# Revit family: Краны шаровые с ЭИМ DN25-50, PN16
name_source: partatom
category: Арматура трубопроводов
revit_build: Autodesk Revit 2015 (Build: 20140322_1515(x64)
units: mm (PartAtom-declared; Revit-internal decimal feet)

## types (4) — shared parameters
URL = http://vogez.by
Видимость клапана = Да
Высота болтов площадки = 6 мм
Высота штока_1 = 25 мм
Высота штока_2 = 70 мм
Диаметр направляющих = 10 мм
Диаметр отверстий = 65 мм
Диаметр патрубка_2 = 45 мм
Диаметр площадки привода_1 = 80 мм
Диаметр площадки привода_2 = 35 мм
Диаметр присоединения привода = 40 мм
Диаметр присоединения провода = 15 мм
Диаметр штока_1 = 30 мм
Диаметр штока_2 = 8 мм
Длина пластины = 112 мм
Изготовитель = ООО "ВОГЕЗЭНЕРГО"
Максимальная температура среды = 150 °C
Материал и цвет корпуса крана = Сталь, неокрашенная
Материал и цвет остальных элементов = Сталь, неокрашенная
Материал и цвет привода = Пластик, черный
Межосевое направляющих = 65 мм
Наименование = Кран шаровой запорно-регулирующий с ЭИМ
Напряжение питания = 220 В
Номинальное время полного хода ВЭП = 90 c
Номинальное давление PN = 1.6 МПа
Номинальное число оборотов = 0.25
Основание пластины = 20 мм
Потребляемая мощность = 15 Вт
Рабочая среда = вода
Расстояние до оси привода_1 = 42 мм
Расстояние до оси привода_2 = 133 мм
Режим работы = повторно-кратковременный, ПВ не более 25%
Сигнал управления = трёхпозиционный
Скругления привода = 25 мм
Степень защиты = IP54
Толщиина пластины = 5 мм
Частота сети = 50 Гц
Ширина пластины = 30 мм
Ширина площадки = 20 мм
Ширина привода = 112 мм

## per-type parameters (varying)
| type | DN | Высота клапана | Высота направляющих | Высота основания привода | Высота посадки привода | Высота с приводом | Диаметр зеркала | Диаметр патрубка_1 | Диаметр узла смешивания | Диаметр фланца | Длина площадки | Масса с приводом | Обозначение | Радиус зеркала | Радиус условный | Радиус фланца | Строительная длина | Тип, марка | Толщина зеркала | Толщина фланца |
| Кран шаровой ВКШР с ЭИМ DN25, PN16 | 25 мм | 30 мм | 75 мм | 85 мм | 35 мм | 155 мм | 71 мм | 50 мм | 68 мм | 120 мм | 58 мм | 7.00 kg | ВКШР DN25 | 36 мм | 13 мм | 60 мм | 160 мм | ВКШР DN25 | 2 мм | 16 мм |
| Кран шаровой ВКШР с ЭИМ DN32, PN16 | 32 мм | 34 мм | 79 мм | 89 мм | 39 мм | 159 мм | 82 мм | 57 мм | 75 мм | 135 мм | 65 мм | 8.00 kg | ВКШР DN32 | 41 мм | 16 мм | 68 мм | 180 мм | ВКШР DN32 | 2 мм | 16 мм |
| Кран шаровой ВКШР с ЭИМ DN40, PN16 | 40 мм | 38 мм | 83 мм | 93 мм | 43 мм | 163 мм | 92 мм | 65 мм | 83 мм | 145 мм | 73 мм | 9.50 kg | ВКШР DN40 | 46 мм | 20 мм | 73 мм | 200 мм | ВКШР DN40 | 3 мм | 17 мм |
| Кран шаровой ВКШР с ЭИМ DN50, PN16 | 50 мм | 43 мм | 88 мм | 98 мм | 48 мм | 168 мм | 107 мм | 75 мм | 93 мм | 160 мм | 83 мм | 12.00 kg | ВКШР DN50 | 54 мм | 25 мм | 80 мм | 230 мм | ВКШР DN50 | 3 мм | 19 мм |
